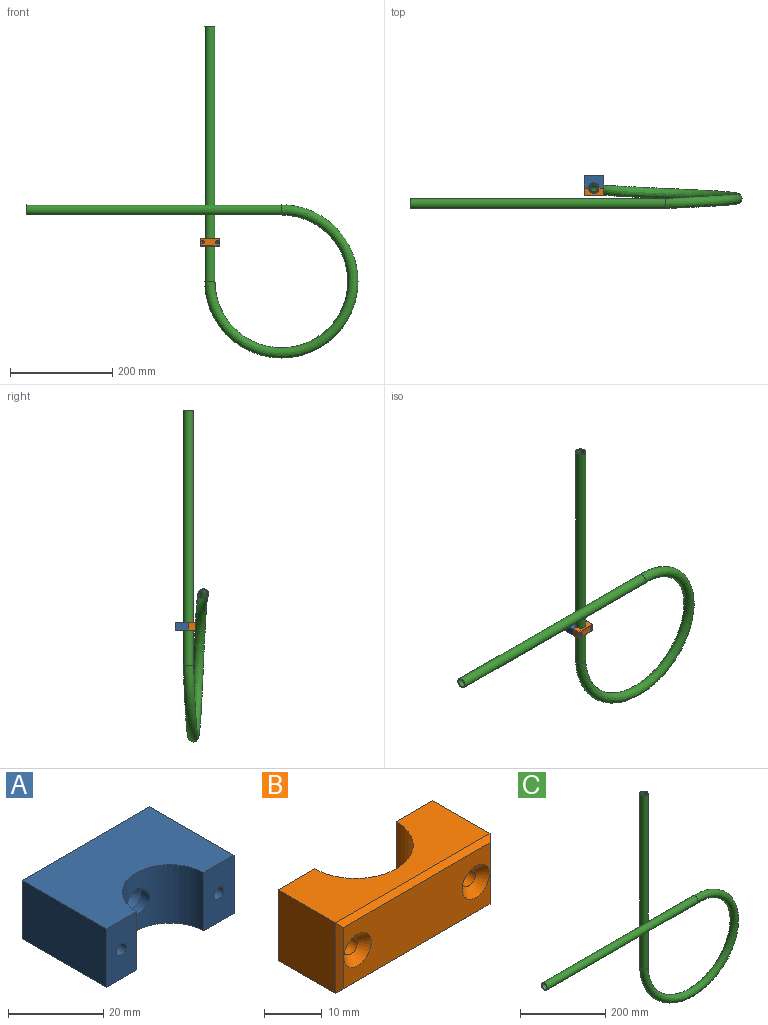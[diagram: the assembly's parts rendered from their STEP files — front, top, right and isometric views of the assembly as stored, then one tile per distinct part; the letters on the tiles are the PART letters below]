
ASSEMBLY  parts=3 mates=2
PART A: 15 faces, bbox 38x25x15 mm
  f0: cylinder r=10mm len=20mm, axis (0,0,-1), area 435.3mm2, adj f3,f4,f6,f7,f8
  f1: plane 38x15mm, normal (0,1,0), area 560.9mm2, adj f2,f5,f6,f7,f9
  f2: plane 25x15mm, normal (-1,0,0), area 375mm2, adj f1,f3,f6,f7
  f3: plane 15x9mm, normal (0,-1,0), area 127.9mm2, adj f0,f2,f6,f7,f14
  f4: plane 15x9mm, normal (0,-1,0), area 127.9mm2, adj f0,f5,f6,f7,f12
  f5: plane 25x15mm, normal (1,0,0), area 375mm2, adj f1,f4,f6,f7
  f6: plane 38x25mm, normal (0,0,1), area 792.9mm2, adj f0,f1,f2,f3,f4,f5
  f7: plane 38x25mm, normal (0,0,-1), area 792.9mm2, adj f0,f1,f2,f3,f4,f5
  f8: cylinder r=3.36mm len=6.72mm, axis (0,1,0), area 48.3mm2, adj f0,f10
  f9: cylinder r=1.7mm len=11.34mm, axis (0,-1,0), area 121.1mm2, adj f1,f10
  f10: cone r=1.7mm half-angle=45deg, axis (0,-1,0), area 37.3mm2, adj f8,f9
  f11: cone r=0mm half-angle=59deg, axis (0,-1,0), area 8.2mm2, adj f12
  f12: cylinder r=1.5mm len=15mm, axis (0,-1,0), area 141.4mm2, adj f4,f11
  f13: cone r=0mm half-angle=59deg, axis (0,-1,0), area 8.2mm2, adj f14
  f14: cylinder r=1.5mm len=15mm, axis (0,-1,0), area 141.4mm2, adj f3,f13
PART B: 16 faces, bbox 38x15x15 mm
  f0: plane 15x9mm, normal (0,1,0), area 125.9mm2, adj f1,f5,f6,f7,f10
  f1: plane 15x14mm, normal (-1,0,0), area 210mm2, adj f0,f6,f7,f15
  f2: plane 36x13mm, normal (0,-1,0), area 397.1mm2, adj f9,f11,f12,f13,f14,f15
  f3: plane 15x14mm, normal (1,0,0), area 210mm2, adj f4,f6,f7,f12
  f4: plane 15x9mm, normal (0,1,0), area 125.9mm2, adj f3,f5,f6,f7,f8
  f5: cylinder r=10mm len=20mm, axis (0,0,-1), area 471.2mm2, adj f0,f4,f6,f7
  f6: plane 38x14mm, normal (0,0,1), area 374.9mm2, adj f0,f1,f3,f4,f5,f13
  f7: plane 38x14mm, normal (0,0,-1), area 374.9mm2, adj f0,f1,f3,f4,f5,f14
  f8: cylinder r=1.7mm len=13.34mm, axis (0,-1,0), area 142.5mm2, adj f4,f9
  f9: cone r=1.7mm half-angle=45deg, axis (0,-1,0), area 37.3mm2, adj f2,f8
  f10: cylinder r=1.7mm len=13.34mm, axis (0,-1,0), area 142.5mm2, adj f0,f11
  f11: cone r=1.7mm half-angle=45deg, axis (0,-1,0), area 37.3mm2, adj f2,f10
  f12: plane 15x1mm, normal (0.71,-0.71,0), area 19.8mm2, adj f2,f3,f13,f14
  f13: plane 38x1mm, normal (0,-0.71,0.71), area 52.3mm2, adj f2,f6,f12,f15
  f14: plane 38x1mm, normal (0,-0.71,-0.71), area 52.3mm2, adj f2,f7,f12,f15
  f15: plane 15x1mm, normal (-0.71,-0.71,0), area 19.8mm2, adj f1,f2,f13,f14
PART C: 8 faces, bbox 650x73.3x650 mm
  f0: cylinder r=8mm len=500mm, axis (0,0,-1), area 25132.7mm2, adj f2,f3
  f1: cylinder r=10mm len=500mm, axis (0,0,-1), area 31415.9mm2, adj f2,f4
  f2: plane 20x20mm, normal (0,0,1), area 113.1mm2, adj f0,f1
  f3: bspline ~296x296mm, area 33182.7mm2, adj f0,f5
  f4: bspline ~300x300mm, area 41478.5mm2, adj f1,f6
  f5: cylinder r=8mm len=500mm, axis (1,0,0), area 25132.7mm2, adj f3,f7
  f6: cylinder r=10mm len=500mm, axis (1,0,0), area 31415.9mm2, adj f4,f7
  f7: plane 20x20mm, normal (-1,0,0), area 113.1mm2, adj f5,f6
PLACE A t=(-227.13,-114.19,66.49)mm
PLACE B t=(-227.13,-102.19,66.49)mm
PLACE C t=(-221.92,-65.91,-2.71)mm
MATE slider A.f0 <-> C.f1  axis (0,0,-1) through (-361.92,-65.91,66.49)mm
MATE fastened B.f8 <-> A.f11  axis (0,1,0) through (-347.42,-65.91,73.99)mm
